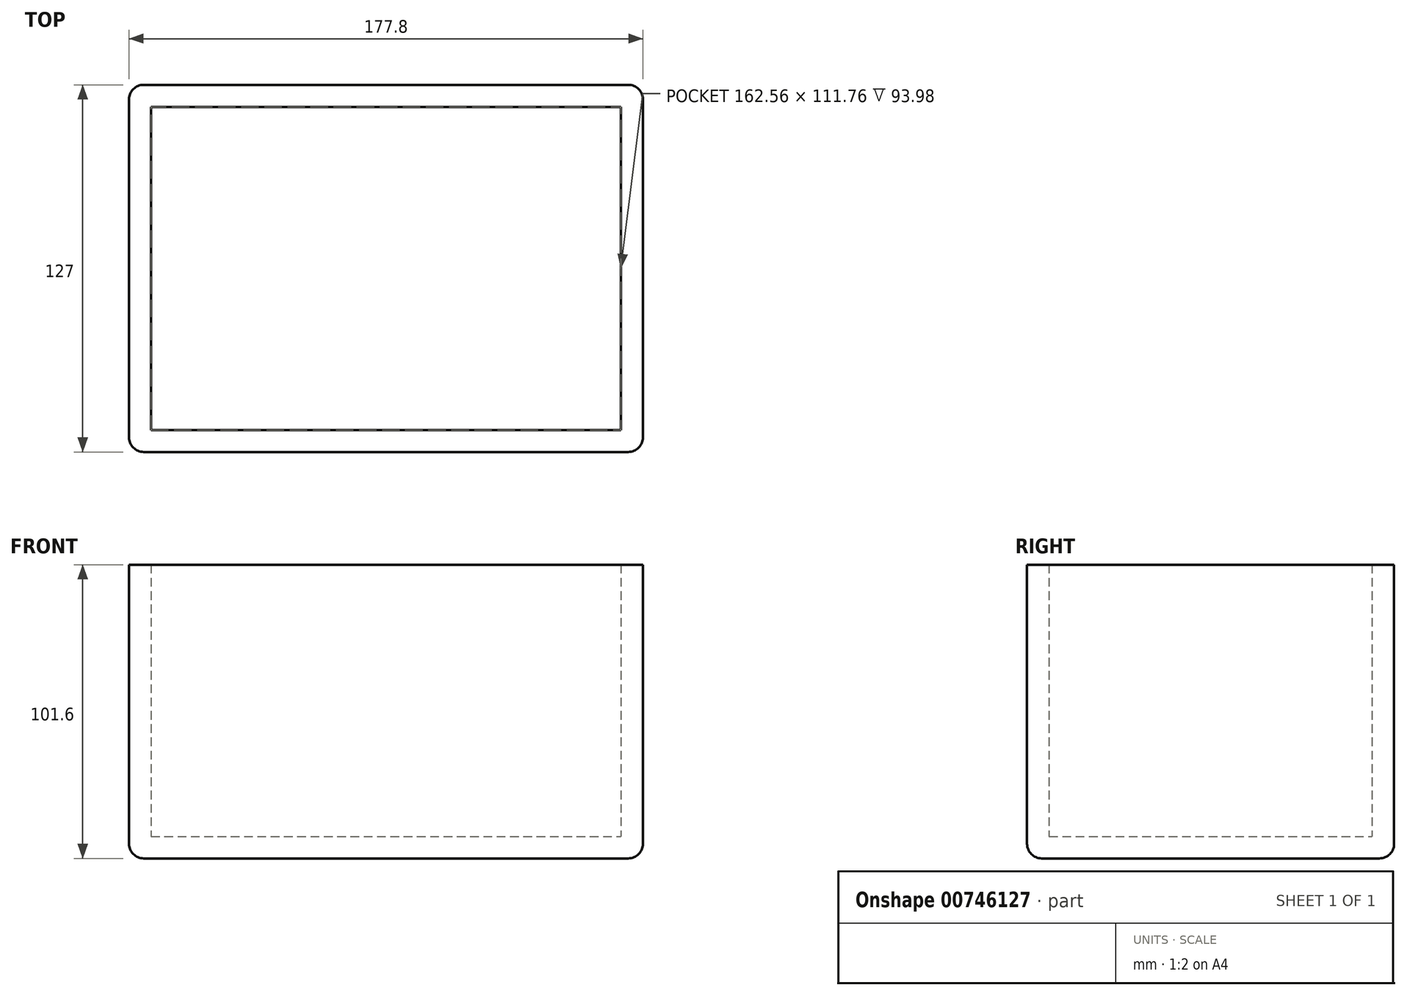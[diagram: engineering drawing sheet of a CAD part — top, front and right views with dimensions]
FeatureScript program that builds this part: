
annotation { "Feature Type Name" : "Feature", "Feature Type Description" : "" }
export const myFeature = defineFeature(function(context is Context, id is Id, definition is map)
    precondition{}
    {
        {
            var Q0;
            Q0=qCreatedBy(makeId("Top.planeOp"),FACE);
            var sketch = newSketch(context, id + "F0", { "sketchPlane" : qUnion([Q0])});
            skLineSegment(sketch, "E0.bottom", {"start": v(-71.31, -37.9) * mm, "end": v(106.49, -37.9) * mm});
            skLineSegment(sketch, "E0.top", {"start": v(-71.31, 89.1) * mm, "end": v(106.49, 89.1) * mm});
            skLineSegment(sketch, "E0.left", {"start": v(-71.31, -37.9) * mm, "end": v(-71.31, 89.1) * mm});
            skLineSegment(sketch, "E0.right", {"start": v(106.49, -37.9) * mm, "end": v(106.49, 89.1) * mm});
            skSolve(sketch);
        }
        {
            var Q0;
            Q0 = qSketchRegion(id + "F0", true);
            extrude(context, id + "F1", {"entities" : qUnion([Q0]), "depth" : 101.6 * mm, "offsetDistance" : 25.4 * mm});
        }
        {
            var Q0;
            Q0=makeQuery(id+"F1.opExtrude","CAP_FACE",FACE,{"disambiguationData":[OSD([sQuery(id+"F0.wireOp",EDGE,"E0.bottom"),sQuery(id+"F0.wireOp",EDGE,"E0.top"),sQuery(id+"F0.wireOp",EDGE,"E0.left"),sQuery(id+"F0.wireOp",EDGE,"E0.right")])],"isStart":false});
            shell(context, id + "F2", {"entities" : qUnion([Q0]), "thickness" : 7.62 * mm});
        }
        {
            var Q0;
            Q0=makeQuery(id+"F1.opExtrude","SWEPT_EDGE",EDGE,{"disambiguationData":[OSD([sQuery(id+"F0.wireOp",EDGE,"E0.bottom"),sQuery(id+"F0.wireOp",EDGE,"E0.left")])]});
            var Q1;
            Q1=makeQuery(id+"F1.opExtrude","CAP_EDGE",EDGE,{"disambiguationData":[OSD([sQuery(id+"F0.wireOp",EDGE,"E0.left")])],"isStart":true});
            var Q2;
            Q2=makeQuery(id+"F1.opExtrude","SWEPT_EDGE",EDGE,{"disambiguationData":[OSD([sQuery(id+"F0.wireOp",EDGE,"E0.top"),sQuery(id+"F0.wireOp",EDGE,"E0.left")])]});
            var Q3;
            Q3=makeQuery(id+"F1.opExtrude","CAP_EDGE",EDGE,{"disambiguationData":[OSD([sQuery(id+"F0.wireOp",EDGE,"E0.top")])],"isStart":true});
            var Q4;
            Q4=makeQuery(id+"F1.opExtrude","SWEPT_EDGE",EDGE,{"disambiguationData":[OSD([sQuery(id+"F0.wireOp",EDGE,"E0.top"),sQuery(id+"F0.wireOp",EDGE,"E0.right")])]});
            var Q5;
            Q5=makeQuery(id+"F1.opExtrude","SWEPT_EDGE",EDGE,{"disambiguationData":[OSD([sQuery(id+"F0.wireOp",EDGE,"E0.bottom"),sQuery(id+"F0.wireOp",EDGE,"E0.right")])]});
            var Q6;
            Q6=makeQuery(id+"F1.opExtrude","CAP_EDGE",EDGE,{"disambiguationData":[OSD([sQuery(id+"F0.wireOp",EDGE,"E0.right")])],"isStart":true});
            var Q7;
            Q7=makeQuery(id+"F1.opExtrude","CAP_EDGE",EDGE,{"disambiguationData":[OSD([sQuery(id+"F0.wireOp",EDGE,"E0.bottom")])],"isStart":true});
            fillet(context, id + "F3", {"entities" : qUnion([Q0, Q1, Q2, Q3, Q4, Q5, Q6, Q7]), "radius" : 5.08 * mm, "tangentPropagation" : true, "allowEdgeOverflow" : false});
        }
    });
